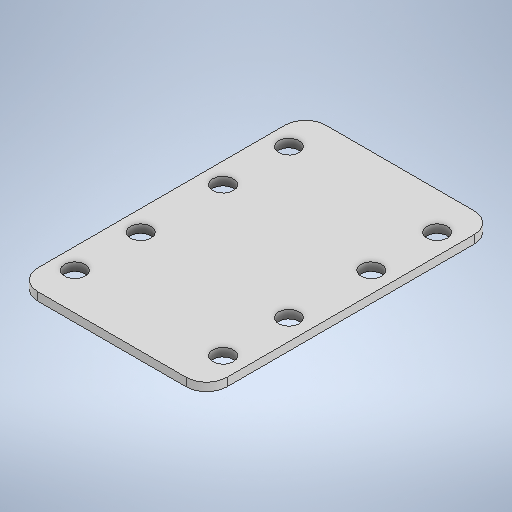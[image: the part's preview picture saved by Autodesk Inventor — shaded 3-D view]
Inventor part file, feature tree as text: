
AUTODESK INVENTOR PART (.ipt)
format: ipt  version: 2025.1 (Build 291241000, 241)  size: 270,336 bytes
history: native  units: mm
features: sketch x2, sheet_metal_op x1, hole x1, fillet x1, mirror x1, other x1
ambient origin geometry x8: Origin, YZ Plane, XZ Plane, XY Plane, X Axis, Y Axis, Z Axis, Center Point
bodies: Solid1 (feature_tree)
feature tree (7):
  sheet_metal_op  "Face1"
  hole  "Hole1"  [1 undecoded]
  fillet  "Fillet1"  Radius=1.0mm
  mirror  "Mirror1"
  sketch  "Sketch1"  dims[d0=23.0mm d1=35.0mm d2=1.0mm]
  other  "Plate1"
  sketch  "Sketch2"  dims[d3=18.0mm d4=9.0mm d5=8.0mm d8=2.5mm d9=2.5mm d10=6.0mm d11=4.0mm d12=2.0mm d13=90.0deg d14=1.0mm d15=20.594885mm d16=2.5mm d17=5.0mm]
note: 1 required parameter value undecoded (feature->parameter linkage not recoverable at this tier; creation-order binding heuristic only, values carry confidence <= 0.55)
